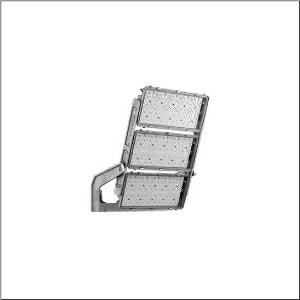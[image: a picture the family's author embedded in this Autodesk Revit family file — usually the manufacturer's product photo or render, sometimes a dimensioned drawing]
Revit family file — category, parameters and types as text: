
# Revit family: floodlight_fl_11_maxi_pro_remote___pl52_5xa779427d01ba_83dd
name_source: partatom
category: Lighting Fixtures
units: mm (PartAtom-declared; Revit-internal decimal feet)

## family parameters
Cut with Voids When Loaded = No
Host = Face
Light Source = No
Part Type = Normal
Room Calculation Point = No
Round Connector Dimension = Use Diameter
Shared = No

## types (1)
- --- (1 x LED, 148130 lm, 1095.9 W, 5000K)
    Apparent Load = 1096 VA
    CIE Flux Codes = 24 55 98 100 100
    Color Rendering = 70
    Color Temperature = 5000K
    Default Elevation = 1800 mm
    Description = Floodlight FL 11  maxi  pro Remote floodlight; light control with lens of PMMA; cover panel of toughened safety glass, transparent; light distribution: PL52, asymmetric direct distribution, LEDcolour temperature: 5000K, rated luminous flux: 148.120lm, colour rendering: CRI > 70, light colour: 750; luminous efficacy: 135lm/W; brightness control: DALI 2 (1 DALI address); with terminal, 8-pole, max. 2.5mm², mains connection: 220..240V/380..400V AC, 50/60Hz, surge voltage resistance: line to ground: 10kV, ECG replaceable separately, LED unit replaceable without ESD environment, dustproof LED module, dimming range 10..100%, no afterglow with DALI off / DMX off command; 1096W floodlight with 3x LED unit of diecast aluminium, coated grey; length: 713mm / width: 651mm / height: 338mm; mounting bracket, of diecast aluminium, uncoated, natural, equipment: Power, protection rating (complete): IP66; insulation class (complete): insulation class I (protective earthing); certification: CE, ENEC, VDE; ball protection: ball impact resistance with accessories, rated ambient temperature 10°C, only for outdoor installations, permissible operating ambient temperature: -40..+40°C, permissible storage temperature: -40..+85°C; packaging unit: 1 piece

Light Distribution: PL52
    Height = 320 mm
    Lamp = 1 x LED
    Lamp Light Flux = 148130 lm
    Lamp Power = 1095.9 W
    Lamp count = 1
    Length = 1002 mm
    Luminous efficacy = 135 lm/W
    Manufacturer = Siteco
    ModVariant = No
    Model = 5XA779427D01BA
    Number of Poles = 1
    OnlyDefault = Yes
    Power Factor = 1
    Product Name = Floodlight FL 11 maxi pro Remote | PL52
    Product group = floodlight | pylon top
    ProductGroupID = 6101
    Protection Class = Protection class I
    Protection Degree = IP 66
    RLX_Detail_Level = 1
    RlxData = <blob elided: 52501 chars, md5=b468a330>
    Socket = socket
    Standby Power = 0 W
    System Light Flux = 148130 lm
    System Power = 1096 W
    Type Comments = factory setting: luminous flux: 100 % | dim-lin: 254 | 760 mA
    Type Image = l_1006784.jpg
    URL = http://relux.com
    VarID = @adj_007505
    Voltage = 0 V
    Weight = 0.00 kg
    Width = 655 mm

## geometry (parser evidence)
native form markers: Blend x4, Sweep x12
no freeform markers — native parametric forms only
